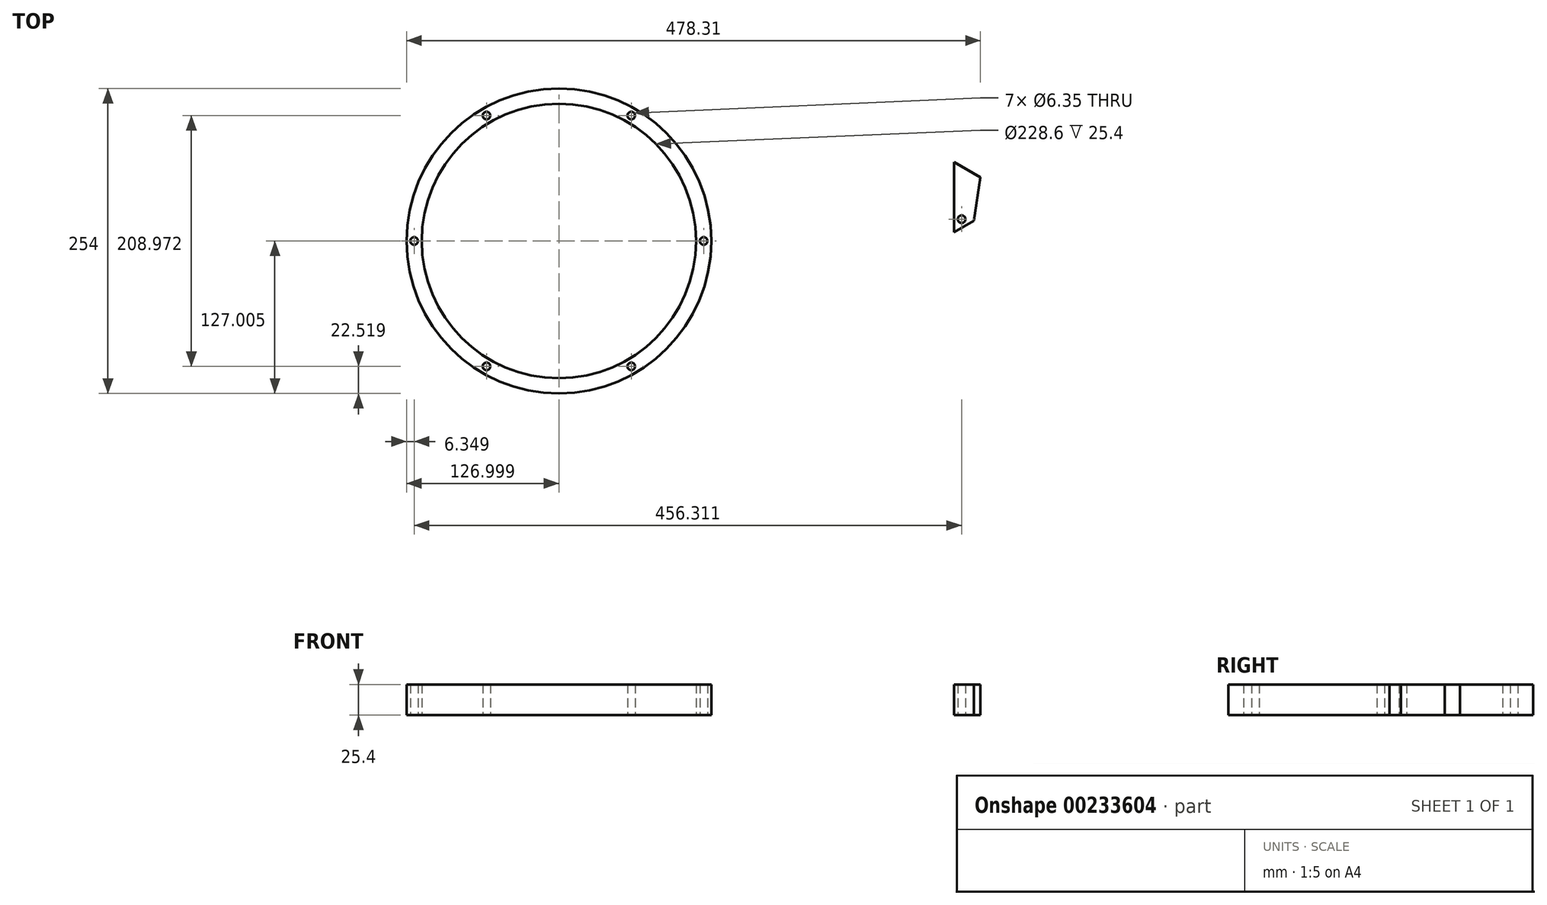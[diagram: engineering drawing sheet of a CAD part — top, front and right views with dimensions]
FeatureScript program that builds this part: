
annotation { "Feature Type Name" : "Feature", "Feature Type Description" : "" }
export const myFeature = defineFeature(function(context is Context, id is Id, definition is map)
    precondition{}
    {
        {
            var Q0;
            Q0=qCreatedBy(makeId("Top.planeOp"),FACE);
            var sketch = newSketch(context, id + "F0", { "sketchPlane" : qUnion([Q0])});
            skCircle(sketch, "E0", {"center": v(0, 0) * mm, "radius": 3.18 * mm});
            skLineSegment(sketch, "E1", {"start": v(44.45, 18.33) * mm, "end": v(-6.35, 47.66) * mm});
            skLineSegment(sketch, "E2", {"start": v(-6.35, 47.66) * mm, "end": v(-6.35, -11) * mm});
            skLineSegment(sketch, "E3", {"start": v(-6.35, -11) * mm, "end": v(44.45, 18.33) * mm});
            skSolve(sketch);
        }
        {
            var Q0;
            Q0 = qSketchRegion(id + "F0", true);
            extrude(context, id + "F1", {"entities" : qUnion([Q0]), "depth" : 25.4 * mm});
        }
        {
            var Q0;
            Q0=makeQuery(id+"F1.opExtrude","CAP_FACE",FACE,{"disambiguationData":[OSD([sQuery(id+"F0.wireOp",EDGE,"E0"),sQuery(id+"F0.wireOp",EDGE,"E1"),sQuery(id+"F0.wireOp",EDGE,"E2"),sQuery(id+"F0.wireOp",EDGE,"E3")])],"isStart":false});
            var sketch = newSketch(context, id + "F2", { "sketchPlane" : qUnion([Q0])});
            skLineSegment(sketch, "E4", {"start": v(10.15, -1.47) * mm, "end": v(15.65, 34.96) * mm});
            skLineSegment(sketch, "E5", {"start": v(15.65, 34.96) * mm, "end": v(44.45, 18.33) * mm});
            skLineSegment(sketch, "E6", {"start": v(44.45, 18.33) * mm, "end": v(10.15, -1.47) * mm});
            skSolve(sketch);
        }
        {
            var Q0;
            Q0 = qSketchRegion(id + "F2", true);
            extrude(context, id + "F3", {"entities" : qUnion([Q0]), "operationType" : NewBodyOperationType.REMOVE, "endBound" : BoundingType.THROUGH_ALL, "oppositeDirection" : true, "depth" : 25.4 * mm});
        }
        {
            var Q0;
            Q0=qCreatedBy(makeId("Top.planeOp"),FACE);
            var sketch = newSketch(context, id + "F4", { "sketchPlane" : qUnion([Q0])});
            skCircle(sketch, "E7", {"center": v(-335.66, -18.15) * mm, "radius": 127 * mm});
            skCircle(sketch, "E8", {"center": v(-335.66, -18.15) * mm, "radius": 114.3 * mm});
            skCircle(sketch, "E9", {"center": v(-215.01, -18.15) * mm, "radius": 3.18 * mm});
            skCircle(sketch, "E10", {"center": v(-456.31, -18.15) * mm, "radius": 3.18 * mm});
            skCircle(sketch, "E11", {"center": v(-395.99, 86.34) * mm, "radius": 3.18 * mm});
            skCircle(sketch, "E12", {"center": v(-275.34, 86.34) * mm, "radius": 3.18 * mm});
            skCircle(sketch, "E13", {"center": v(-275.34, -122.63) * mm, "radius": 3.18 * mm});
            skCircle(sketch, "E14", {"center": v(-395.99, -122.63) * mm, "radius": 3.18 * mm});
            skLineSegment(sketch, "E15", {"start": v(-335.66, -18.15) * mm, "end": v(-275.34, 86.34) * mm, "construction": true});
            skLineSegment(sketch, "E16", {"start": v(-335.66, -18.15) * mm, "end": v(-215.01, -18.15) * mm, "construction": true});
            skLineSegment(sketch, "E17", {"start": v(-335.66, -18.15) * mm, "end": v(-275.34, -122.63) * mm, "construction": true});
            skLineSegment(sketch, "E18", {"start": v(-335.66, -18.15) * mm, "end": v(-395.99, -122.63) * mm, "construction": true});
            skLineSegment(sketch, "E19", {"start": v(-335.66, -18.15) * mm, "end": v(-456.31, -18.15) * mm, "construction": true});
            skLineSegment(sketch, "E20", {"start": v(-335.66, -18.15) * mm, "end": v(-395.99, 86.34) * mm, "construction": true});
            skCircle(sketch, "E21", {"center": v(-335.66, -18.15) * mm, "radius": 120.65 * mm, "construction": true});
            skSolve(sketch);
        }
        {
            var Q0;
            Q0 = qSketchRegion(id + "F4", true);
            extrude(context, id + "F5", {"entities" : qUnion([Q0]), "depth" : 25.4 * mm});
        }
    });
